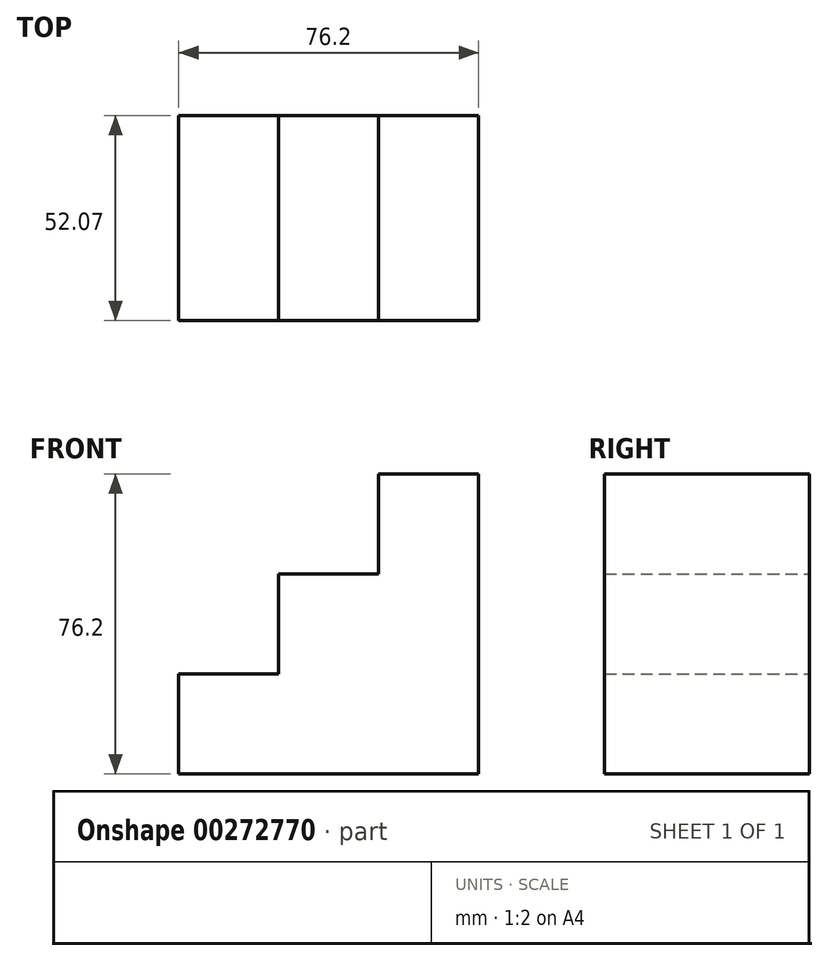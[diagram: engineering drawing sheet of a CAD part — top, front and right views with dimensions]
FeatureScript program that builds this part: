
annotation { "Feature Type Name" : "Feature", "Feature Type Description" : "" }
export const myFeature = defineFeature(function(context is Context, id is Id, definition is map)
    precondition{}
    {
        {
            var Q0;
            Q0=qCreatedBy(makeId("Front.planeOp"),FACE);
            var sketch = newSketch(context, id + "F0", { "sketchPlane" : qUnion([Q0])});
            skLineSegment(sketch, "E0", {"start": v(-49.1, -15.45) * mm, "end": v(27.1, -15.45) * mm});
            skLineSegment(sketch, "E1", {"start": v(27.1, -15.45) * mm, "end": v(27.1, 60.75) * mm});
            skLineSegment(sketch, "E2", {"start": v(27.1, 60.75) * mm, "end": v(1.7, 60.75) * mm});
            skLineSegment(sketch, "E3", {"start": v(1.7, 60.75) * mm, "end": v(1.7, 35.35) * mm});
            skLineSegment(sketch, "E4", {"start": v(1.7, 35.35) * mm, "end": v(-23.7, 35.35) * mm});
            skLineSegment(sketch, "E5", {"start": v(-23.7, 35.35) * mm, "end": v(-23.7, 9.95) * mm});
            skLineSegment(sketch, "E6", {"start": v(-23.7, 9.95) * mm, "end": v(-49.1, 9.95) * mm});
            skLineSegment(sketch, "E7", {"start": v(-49.1, 9.95) * mm, "end": v(-49.1, -15.45) * mm});
            skSolve(sketch);
        }
        {
            var Q0;
            Q0 = qSketchRegion(id + "F0", true);
            extrude(context, id + "F1", {"entities" : qUnion([Q0]), "depth" : 52.07 * mm});
        }
    });
